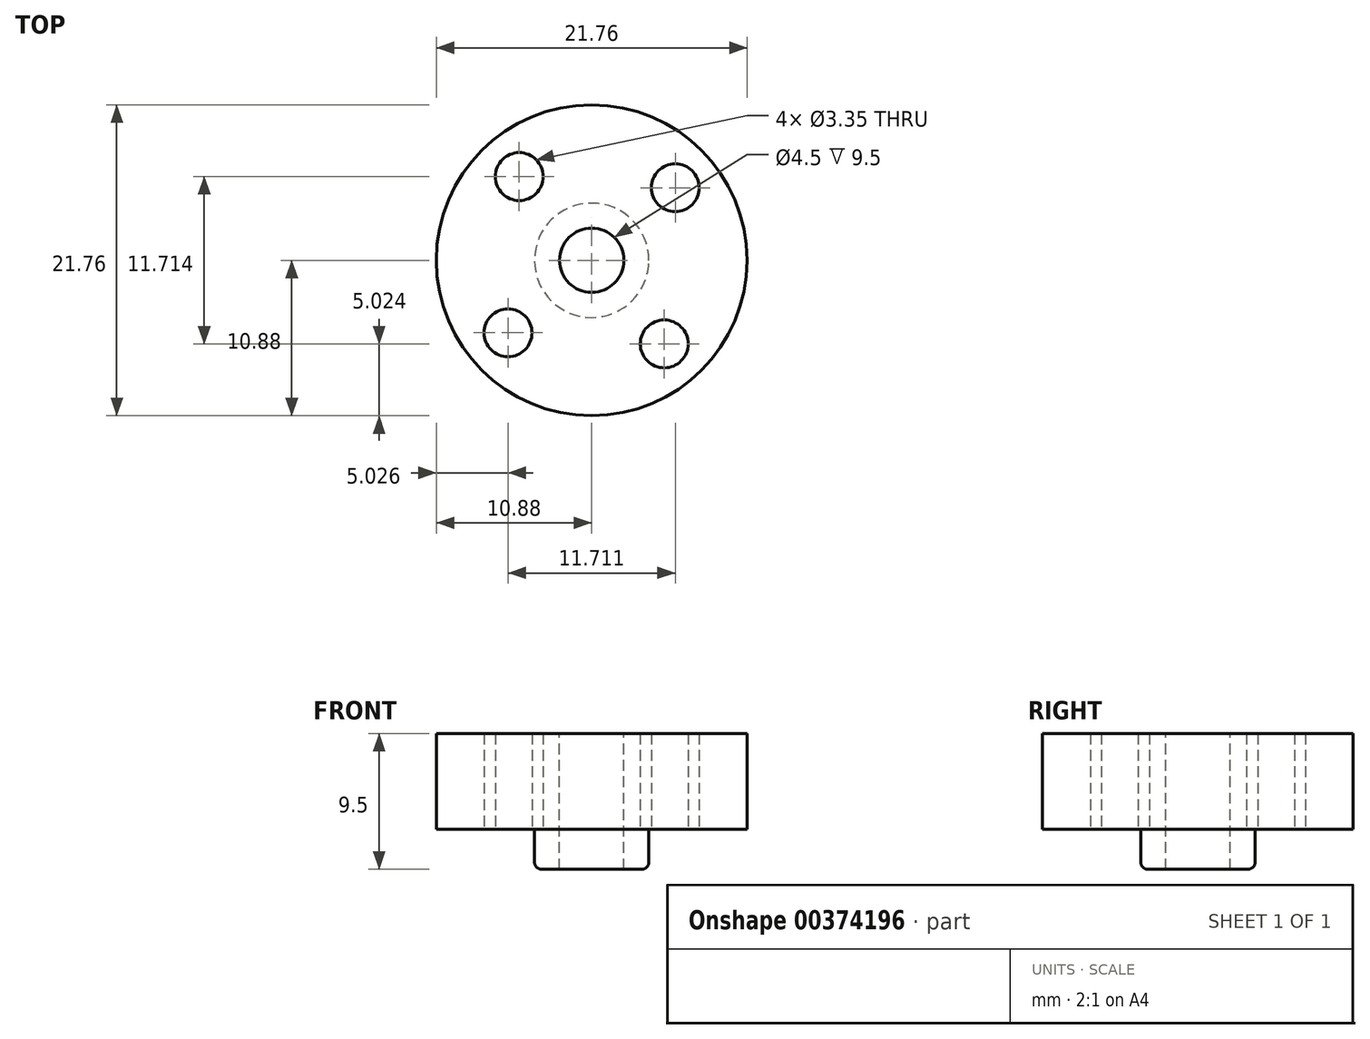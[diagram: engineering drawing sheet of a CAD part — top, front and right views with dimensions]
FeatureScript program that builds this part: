
annotation { "Feature Type Name" : "Feature", "Feature Type Description" : "" }
export const myFeature = defineFeature(function(context is Context, id is Id, definition is map)
    precondition{}
    {
        {
            var Q0;
            Q0=qCreatedBy(makeId("Top.planeOp"),FACE);
            var sketch = newSketch(context, id + "F0", { "sketchPlane" : qUnion([Q0])});
            skCircle(sketch, "E0", {"center": v(0, 0) * mm, "radius": 10.88 * mm});
            skLineSegment(sketch, "E1", {"start": v(7.12, -8.22) * mm, "end": v(-7.12, 8.22) * mm, "construction": true});
            skLineSegment(sketch, "E2", {"start": v(0, 0) * mm, "end": v(8.22, 7.12) * mm, "construction": true});
            skCircle(sketch, "E3", {"center": v(5.86, 5.08) * mm, "radius": 1.68 * mm});
            skCircle(sketch, "E4", {"center": v(5.08, -5.86) * mm, "radius": 1.68 * mm});
            skCircle(sketch, "E5", {"center": v(-5.07, 5.86) * mm, "radius": 1.68 * mm});
            skCircle(sketch, "E6.MirrorC", {"center": v(-5.85, -5.07) * mm, "radius": 1.68 * mm});
            skSolve(sketch);
        }
        {
            var Q0;
            Q0=makeQuery(id+"F0.imprint","IMPRINT",FACE,{"disambiguationData":[TD([[makeQuery(id+"F0.imprint","IMPRINT",EDGE,{"derivedFrom":sQuery(id+"F0.wireOp",EDGE,"E0")}),1.0]])]});
            extrude(context, id + "F1", {"entities" : qUnion([Q0]), "depth" : 6.7 * mm});
        }
        {
            var Q0;
            Q0=qCreatedBy(makeId("Top.planeOp"),FACE);
            var sketch = newSketch(context, id + "F2", { "sketchPlane" : qUnion([Q0])});
            skCircle(sketch, "E7", {"center": v(0, 0) * mm, "radius": 4 * mm});
            skSolve(sketch);
        }
        {
            var Q0;
            Q0=makeQuery(id+"F2.imprint","IMPRINT",FACE,{"disambiguationData":[TD([[makeQuery(id+"F2.imprint","IMPRINT",EDGE,{"derivedFrom":sQuery(id+"F2.wireOp",EDGE,"E7")}),1.0]])]});
            extrude(context, id + "F3", {"entities" : qUnion([Q0]), "operationType" : NewBodyOperationType.ADD, "oppositeDirection" : true, "depth" : 2.8 * mm});
        }
        {
            var Q0;
            Q0=qCreatedBy(makeId("Top.planeOp"),FACE);
            var sketch = newSketch(context, id + "F4", { "sketchPlane" : qUnion([Q0])});
            skCircle(sketch, "E8", {"center": v(0, 0) * mm, "radius": 2.25 * mm});
            skSolve(sketch);
        }
        {
            var Q0;
            Q0=makeQuery(id+"F4.imprint","IMPRINT",FACE,{"disambiguationData":[TD([[makeQuery(id+"F4.imprint","IMPRINT",EDGE,{"derivedFrom":sQuery(id+"F4.wireOp",EDGE,"E8")}),1.0]])]});
            extrude(context, id + "F5", {"entities" : qUnion([Q0]), "operationType" : NewBodyOperationType.REMOVE, "endBound" : BoundingType.SYMMETRIC, "oppositeDirection" : true, "depth" : 25 * mm});
        }
        {
            var Q0;
            Q0=makeQuery(id+"F3.opExtrude","CAP_EDGE",EDGE,{"disambiguationData":[OSD([sQuery(id+"F2.wireOp",EDGE,"E7")])],"isStart":false});
            fillet(context, id + "F6", {"entities" : qUnion([Q0]), "radius" : .5 * mm, "tangentPropagation" : true, "allowEdgeOverflow" : false});
        }
    });
